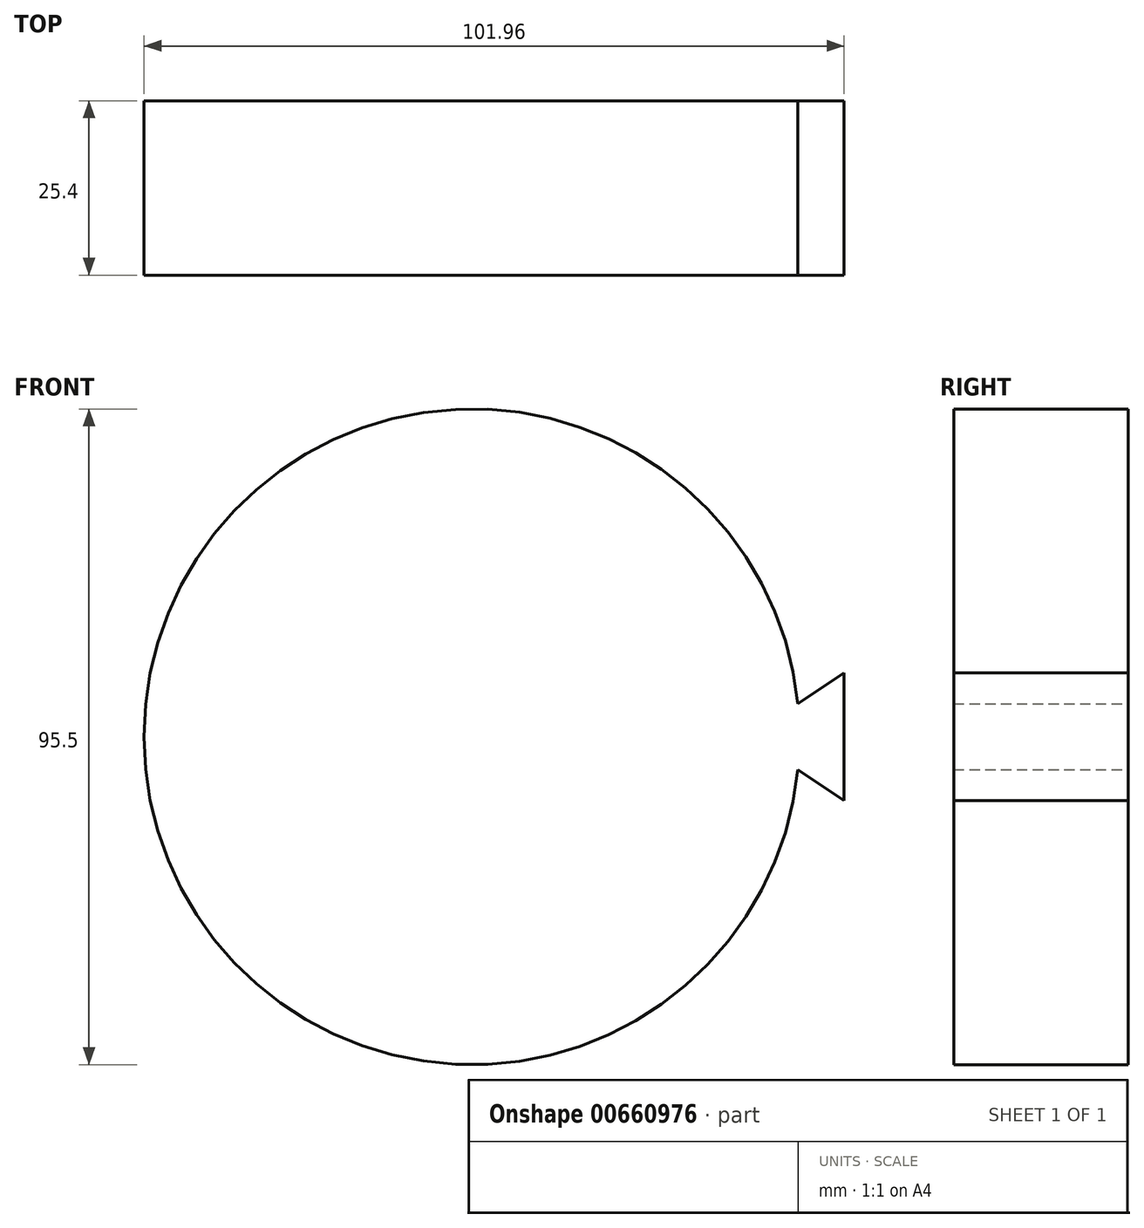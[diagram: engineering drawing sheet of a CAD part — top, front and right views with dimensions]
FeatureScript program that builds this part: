
annotation { "Feature Type Name" : "Feature", "Feature Type Description" : "" }
export const myFeature = defineFeature(function(context is Context, id is Id, definition is map)
    precondition{}
    {
        {
            var Q0;
            Q0=qCreatedBy(makeId("Front.planeOp"),FACE);
            var sketch = newSketch(context, id + "F0", { "sketchPlane" : qUnion([Q0])});
            skCircle(sketch, "E0", {"center": v(0, 0) * mm, "radius": 47.75 * mm});
            skLineSegment(sketch, "E1", {"start": v(40.46, 0) * mm, "end": v(54.2, 9.31) * mm});
            skLineSegment(sketch, "E2", {"start": v(54.2, 9.31) * mm, "end": v(54.2, -9.31) * mm});
            skLineSegment(sketch, "E3", {"start": v(54.2, -9.31) * mm, "end": v(40.46, 0) * mm});
            skSolve(sketch);
        }
        {
            var Q0;
            {var subQ0=sQuery(id+"F0.wireOp",EDGE,"E1");var subQ1=sQuery(id+"F0.wireOp",EDGE,"E0");var subQ2=makeQuery(id+"F0.imprint","INTERSECT",VERTEX,{"derivedFrom":[subQ1,subQ0]});Q0=makeQuery(id+"F0.imprint","IMPRINT",FACE,{"disambiguationData":[TD([[makeQuery(id+"F0.imprint","IMPRINT",EDGE,{"disambiguationData":[TD([[subQ2,-1.0]])],"derivedFrom":subQ1}),1.0]])]});}
            var Q1;
            {var subQ0=sQuery(id+"F0.wireOp",EDGE,"E1");var subQ1=sQuery(id+"F0.wireOp",EDGE,"E0");var subQ2=makeQuery(id+"F0.imprint","INTERSECT",VERTEX,{"derivedFrom":[subQ1,subQ0]});Q1=makeQuery(id+"F0.imprint","IMPRINT",FACE,{"disambiguationData":[TD([[makeQuery(id+"F0.imprint","IMPRINT",EDGE,{"disambiguationData":[TD([[subQ2,1.0]])],"derivedFrom":subQ1}),1.0]])]});}
            var Q2;
            {var subQ5=sQuery(id+"F0.wireOp",EDGE,"E2");Q2=makeQuery(id+"F0.imprint","IMPRINT",FACE,{"disambiguationData":[TD([[makeQuery(id+"F0.imprint","IMPRINT",EDGE,{"derivedFrom":subQ5}),-1.0]])]});}
            extrude(context, id + "F1", {"entities" : qUnion([Q0, Q1, Q2]), "depth" : 25.4 * mm, "offsetDistance" : 25.4 * mm});
        }
    });
